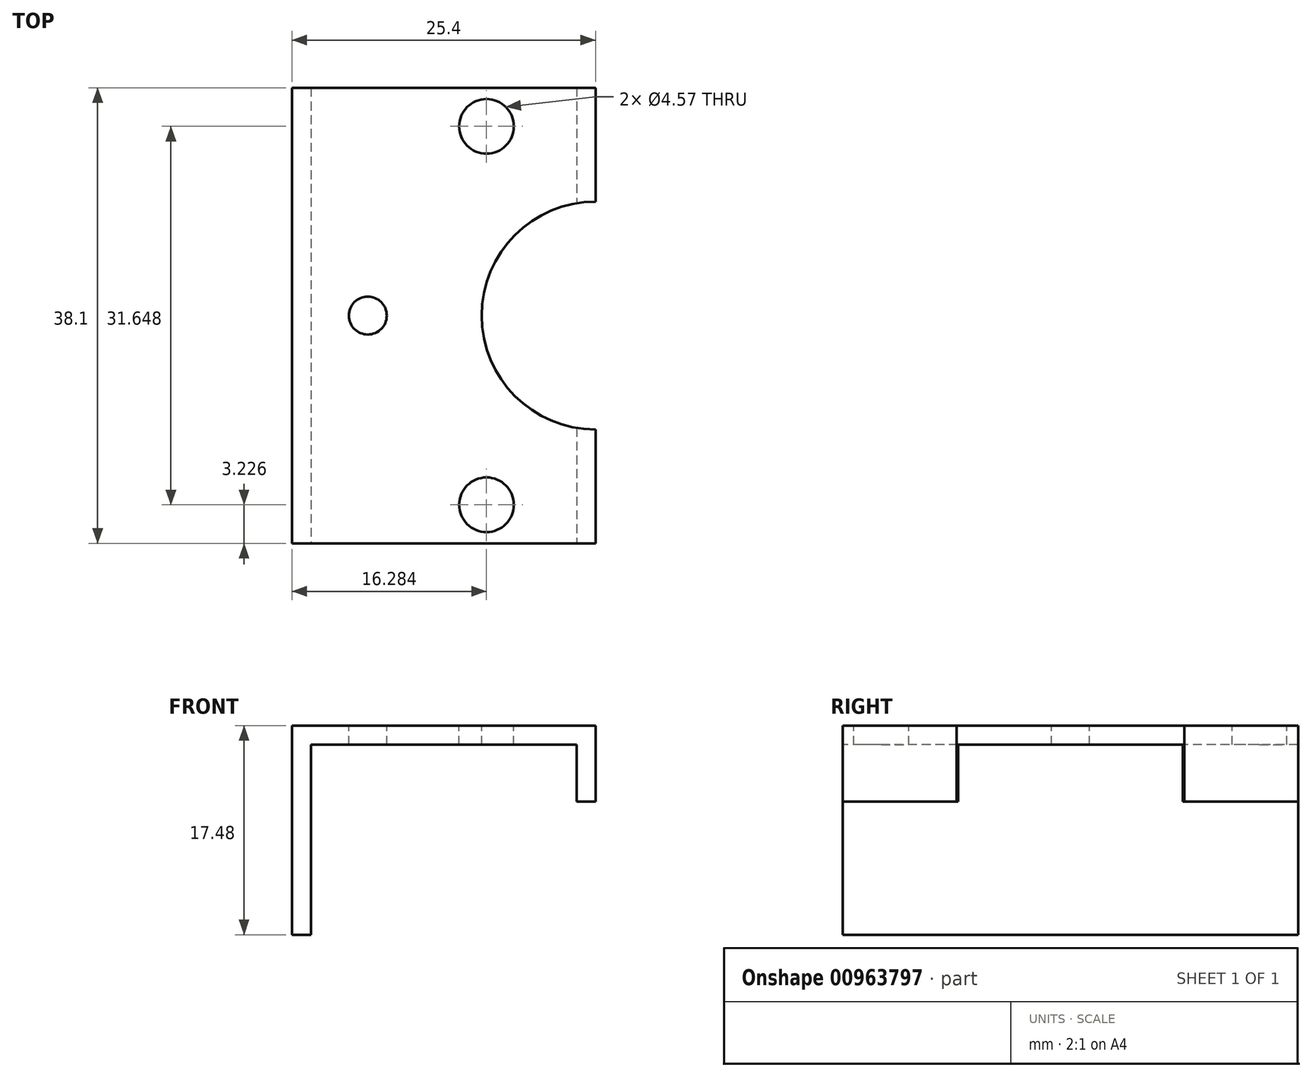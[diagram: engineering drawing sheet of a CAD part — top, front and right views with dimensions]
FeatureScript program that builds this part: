
annotation { "Feature Type Name" : "Feature", "Feature Type Description" : "" }
export const myFeature = defineFeature(function(context is Context, id is Id, definition is map)
    precondition{}
    {
        {
            var Q0;
            Q0=qCreatedBy(makeId("Front.planeOp"),FACE);
            var sketch = newSketch(context, id + "F0", { "sketchPlane" : qUnion([Q0])});
            skLineSegment(sketch, "E0", {"start": v(0, 0) * mm, "end": v(0, 11.13) * mm, "construction": true});
            skLineSegment(sketch, "E1", {"start": v(0, 11.13) * mm, "end": v(16.88, 11.13) * mm, "construction": true});
            skLineSegment(sketch, "E2", {"start": v(9.12, 16.82) * mm, "end": v(9.12, -7.6) * mm, "construction": true});
            skLineSegment(sketch, "E3", {"start": v(-15.49, 17.48) * mm, "end": v(9.91, 17.48) * mm});
            skLineSegment(sketch, "E4", {"start": v(9.91, 17.48) * mm, "end": v(9.91, 11.13) * mm});
            skLineSegment(sketch, "E5", {"start": v(-15.49, 17.48) * mm, "end": v(-15.49, 0) * mm});
            skLineSegment(sketch, "E6", {"start": v(-15.49, 0) * mm, "end": v(-13.9, 0) * mm});
            skLineSegment(sketch, "E7", {"start": v(-13.9, 0) * mm, "end": v(-13.9, 15.89) * mm});
            skLineSegment(sketch, "E8", {"start": v(-13.9, 15.89) * mm, "end": v(8.32, 15.89) * mm});
            skLineSegment(sketch, "E9", {"start": v(8.32, 15.89) * mm, "end": v(8.32, 11.13) * mm});
            skLineSegment(sketch, "E10", {"start": v(8.32, 11.13) * mm, "end": v(9.91, 11.13) * mm});
            skSolve(sketch);
        }
        {
            var Q0;
            Q0=makeQuery(id+"F0.imprint","IMPRINT",FACE,{"disambiguationData":[TD([[makeQuery(id+"F0.imprint","IMPRINT",EDGE,{"derivedFrom":sQuery(id+"F0.wireOp",EDGE,"E3")}),-1.0]])]});
            extrude(context, id + "F1", {"entities" : qUnion([Q0]), "oppositeDirection" : true, "depth" : 38.1 * mm, "offsetDistance" : 25.4 * mm});
        }
        {
            var Q0;
            Q0=makeQuery(id+"F1.opExtrude","SWEPT_FACE",FACE,{"disambiguationData":[OSD([sQuery(id+"F0.wireOp",EDGE,"E3")])]});
            var sketch = newSketch(context, id + "F2", { "sketchPlane" : qUnion([Q0])});
            skLineSegment(sketch, "E11", {"start": v(9.91, 19.05) * mm, "end": v(-15.49, 19.05) * mm, "construction": true});
            skLineSegment(sketch, "E12", {"start": v(0.8, 3.1) * mm, "end": v(0.8, 34.87) * mm});
            skLineSegment(sketch, "E13", {"start": v(7.92, 34.87) * mm, "end": v(-10.45, 34.87) * mm});
            skLineSegment(sketch, "E14", {"start": v(8.02, 3.23) * mm, "end": v(-11.35, 3.23) * mm});
            skCircle(sketch, "E15", {"center": v(0.8, 34.87) * mm, "radius": 2.29 * mm});
            skCircle(sketch, "E16", {"center": v(0.8, 3.23) * mm, "radius": 2.29 * mm});
            skCircle(sketch, "E17", {"center": v(9.91, 19.05) * mm, "radius": 9.53 * mm});
            skCircle(sketch, "E18", {"center": v(-9.14, 19.05) * mm, "radius": 1.59 * mm});
            skSolve(sketch);
        }
        {
            var Q0;
            Q0 = qSketchRegion(id + "F2", true);
            extrude(context, id + "F3", {"entities" : qUnion([Q0]), "operationType" : NewBodyOperationType.REMOVE, "endBound" : BoundingType.THROUGH_ALL, "oppositeDirection" : true, "depth" : 25.4 * mm, "offsetDistance" : 25.4 * mm});
        }
    });
